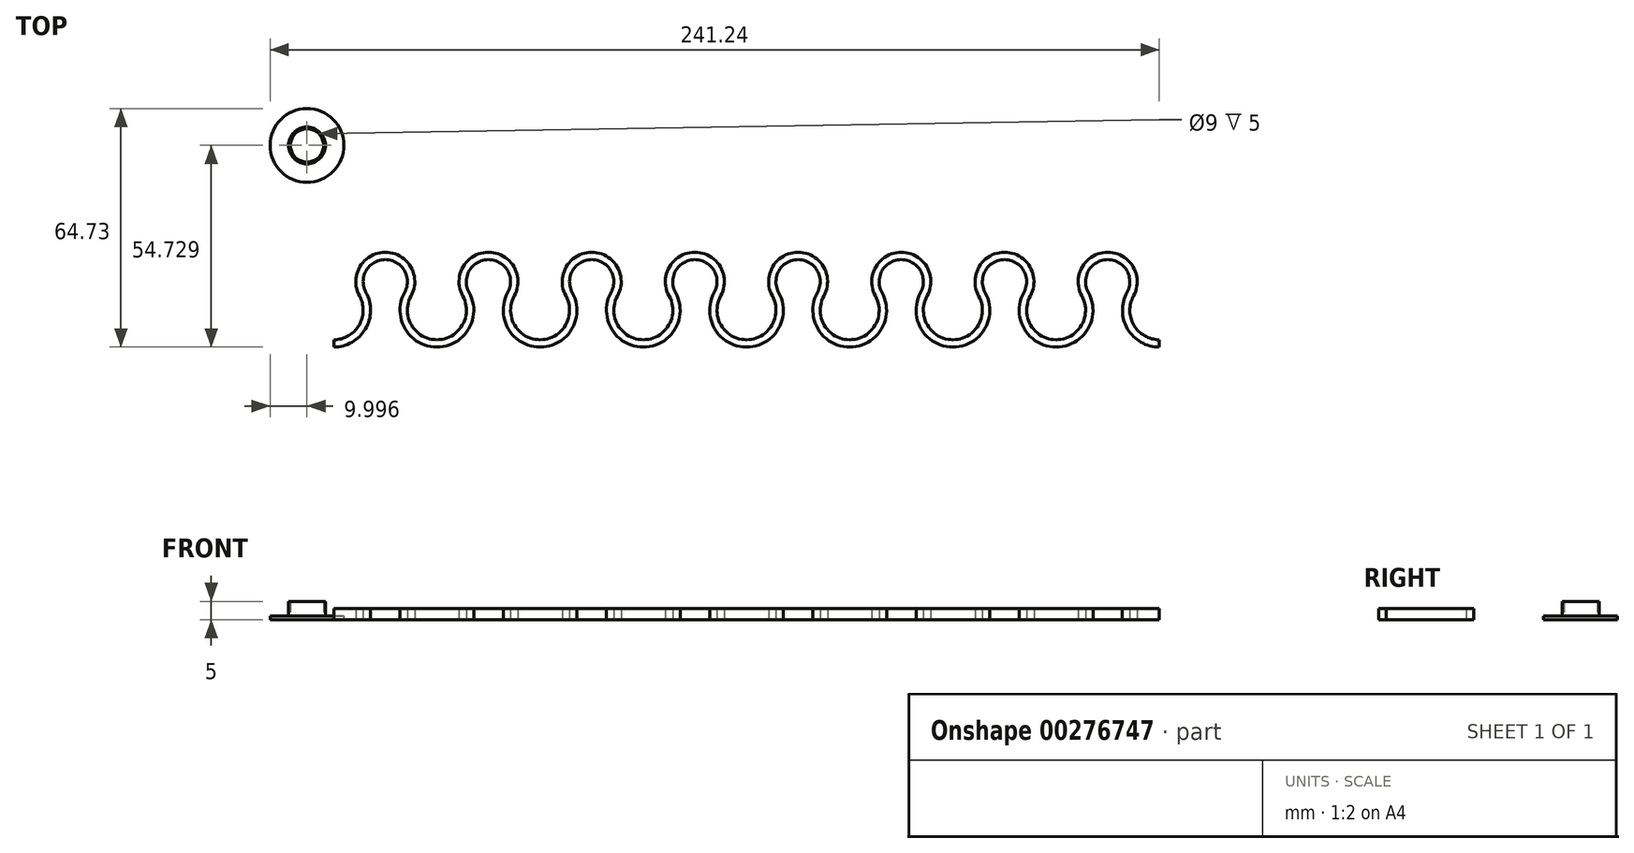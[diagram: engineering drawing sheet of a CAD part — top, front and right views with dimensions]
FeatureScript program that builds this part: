
annotation { "Feature Type Name" : "Feature", "Feature Type Description" : "" }
export const myFeature = defineFeature(function(context is Context, id is Id, definition is map)
    precondition{}
    {
        {
            var Q0;
            Q0=qCreatedBy(makeId("Top.planeOp"),FACE);
            var sketch = newSketch(context, id + "F0", { "sketchPlane" : qUnion([Q0])});
            skPoint(sketch, "E0", {"position": v(14, 0) * mm});
            skPoint(sketch, "E1", {"position": v(28, 0) * mm});
            skArc(sketch, "E2", {"start": v(0, 0) * mm, "mid": v(7, 11.87) * mm, "end": v(14, 0) * mm});
            skArc(sketch, "E3", {"start": v(14, 0) * mm, "mid": v(21, -11.87) * mm, "end": v(28, 0) * mm});
            skArc(sketch, "E4.1.0.0", {"start": v(28, 0) * mm, "mid": v(35, 11.87) * mm, "end": v(42, 0) * mm});
            skArc(sketch, "E4.1.0.1", {"start": v(42, 0) * mm, "mid": v(49, -11.87) * mm, "end": v(56, 0) * mm});
            skArc(sketch, "E4.2.0.0", {"start": v(56, 0) * mm, "mid": v(63, 11.87) * mm, "end": v(70, 0) * mm});
            skArc(sketch, "E4.2.0.1", {"start": v(70, 0) * mm, "mid": v(77, -11.87) * mm, "end": v(84, 0) * mm});
            skArc(sketch, "E4.3.0.0", {"start": v(84, 0) * mm, "mid": v(91, 11.87) * mm, "end": v(98, 0) * mm});
            skArc(sketch, "E4.3.0.1", {"start": v(98, 0) * mm, "mid": v(105, -11.87) * mm, "end": v(112, 0) * mm});
            skArc(sketch, "E4.4.0.0", {"start": v(112, 0) * mm, "mid": v(119, 11.87) * mm, "end": v(126, 0) * mm});
            skArc(sketch, "E4.4.0.1", {"start": v(126, 0) * mm, "mid": v(133, -11.87) * mm, "end": v(140, 0) * mm});
            skArc(sketch, "E4.5.0.0", {"start": v(140, 0) * mm, "mid": v(147, 11.87) * mm, "end": v(154, 0) * mm});
            skArc(sketch, "E4.5.0.1", {"start": v(154, 0) * mm, "mid": v(161, -11.87) * mm, "end": v(168, 0) * mm});
            skArc(sketch, "E4.6.0.0", {"start": v(168, 0) * mm, "mid": v(175, 11.87) * mm, "end": v(182, 0) * mm});
            skArc(sketch, "E4.6.0.1", {"start": v(182, 0) * mm, "mid": v(189, -11.87) * mm, "end": v(196, 0) * mm});
            skArc(sketch, "E4.7.0.0", {"start": v(196, 0) * mm, "mid": v(203, 11.87) * mm, "end": v(210, 0) * mm});
            skArc(sketch, "E4.7.0.1", {"start": v(210, 0) * mm, "mid": v(217, -11.87) * mm, "end": v(224, 0) * mm});
            skArc(sketch, "E4.8.0.0", {"start": v(224, 0) * mm, "mid": v(231, 11.87) * mm, "end": v(238, 0) * mm});
            skArc(sketch, "E4.8.0.1", {"start": v(238, 0) * mm, "mid": v(245, -11.87) * mm, "end": v(252, 0) * mm});
            skArc(sketch, "E4.9.0.0", {"start": v(252, 0) * mm, "mid": v(259, 11.87) * mm, "end": v(266, 0) * mm});
            skArc(sketch, "E4.9.0.1", {"start": v(266, 0) * mm, "mid": v(273, -11.87) * mm, "end": v(280, 0) * mm});
            skLineSegment(sketch, "E4.direction1", {"start": v(0, 0) * mm, "end": v(28, 0) * mm, "construction": true});
            skArc(sketch, "E5.0", {"start": v(264.25, 0.97) * mm, "mid": v(273, -13.87) * mm, "end": v(281.75, 0.97) * mm});
            skArc(sketch, "E5.1", {"start": v(253.75, 0.97) * mm, "mid": v(259, 9.87) * mm, "end": v(264.25, 0.97) * mm});
            skArc(sketch, "E5.2", {"start": v(236.25, 0.97) * mm, "mid": v(245, -13.87) * mm, "end": v(253.75, 0.97) * mm});
            skArc(sketch, "E5.3", {"start": v(225.75, 0.97) * mm, "mid": v(231, 9.87) * mm, "end": v(236.25, 0.97) * mm});
            skArc(sketch, "E5.4", {"start": v(208.25, 0.97) * mm, "mid": v(217, -13.87) * mm, "end": v(225.75, 0.97) * mm});
            skArc(sketch, "E5.5", {"start": v(197.75, 0.97) * mm, "mid": v(203, 9.87) * mm, "end": v(208.25, 0.97) * mm});
            skArc(sketch, "E5.6", {"start": v(180.25, 0.97) * mm, "mid": v(189, -13.87) * mm, "end": v(197.75, 0.97) * mm});
            skArc(sketch, "E5.7", {"start": v(169.75, 0.97) * mm, "mid": v(175, 9.87) * mm, "end": v(180.25, 0.97) * mm});
            skArc(sketch, "E5.8", {"start": v(152.25, 0.97) * mm, "mid": v(161, -13.87) * mm, "end": v(169.75, 0.97) * mm});
            skArc(sketch, "E5.9", {"start": v(57.75, 0.97) * mm, "mid": v(63, 9.87) * mm, "end": v(68.25, 0.97) * mm});
            skArc(sketch, "E5.10", {"start": v(40.25, 0.97) * mm, "mid": v(49, -13.87) * mm, "end": v(57.75, 0.97) * mm});
            skArc(sketch, "E5.11", {"start": v(29.75, 0.97) * mm, "mid": v(35, 9.87) * mm, "end": v(40.25, 0.97) * mm});
            skArc(sketch, "E5.12", {"start": v(12.25, 0.97) * mm, "mid": v(21, -13.87) * mm, "end": v(29.75, 0.97) * mm});
            skArc(sketch, "E5.13", {"start": v(68.25, 0.97) * mm, "mid": v(77, -13.87) * mm, "end": v(85.75, 0.97) * mm});
            skArc(sketch, "E5.14", {"start": v(85.75, 0.97) * mm, "mid": v(91, 9.87) * mm, "end": v(96.25, 0.97) * mm});
            skArc(sketch, "E5.15", {"start": v(96.25, 0.97) * mm, "mid": v(105, -13.87) * mm, "end": v(113.75, 0.97) * mm});
            skArc(sketch, "E5.16", {"start": v(113.75, 0.97) * mm, "mid": v(119, 9.87) * mm, "end": v(124.25, 0.97) * mm});
            skArc(sketch, "E5.17", {"start": v(124.25, 0.97) * mm, "mid": v(133, -13.87) * mm, "end": v(141.75, 0.97) * mm});
            skArc(sketch, "E5.18", {"start": v(141.75, 0.97) * mm, "mid": v(147, 9.87) * mm, "end": v(152.25, 0.97) * mm});
            skLineSegment(sketch, "E6", {"start": v(21, -3.87) * mm, "end": v(21, -64.76) * mm});
            skPoint(sketch, "E6.endSnap0", {"position": v(21, -11.87) * mm});
            skLineSegment(sketch, "E7", {"start": v(21, -64.76) * mm, "end": v(273, -64.76) * mm});
            skLineSegment(sketch, "E8", {"start": v(273, -3.87) * mm, "end": v(273, -64.76) * mm});
            skLineSegment(sketch, "E9", {"start": v(245, -3.87) * mm, "end": v(245, -64.76) * mm});
            skPoint(sketch, "E9.endSnap0", {"position": v(245, -11.87) * mm});
            skLineSegment(sketch, "E10", {"start": v(245, -64.76) * mm, "end": v(246.72, -66.87) * mm});
            skSolve(sketch);
        }
        {
            var Q0;
            {var subQ1=sQuery(id+"F0.wireOp",EDGE,"E5.3");Q0=makeQuery(id+"F0.imprint","IMPRINT",FACE,{"disambiguationData":[TD([[makeQuery(id+"F0.imprint","IMPRINT",EDGE,{"derivedFrom":subQ1}),-1.0]])]});}
            extrude(context, id + "F1", {"entities" : qUnion([Q0]), "depth" : 3 * mm});
        }
        {
            var Q0;
            Q0=qCreatedBy(makeId("Top.planeOp"),FACE);
            var sketch = newSketch(context, id + "F2", { "sketchPlane" : qUnion([Q0])});
            skCircle(sketch, "E11", {"center": v(13.76, 40.86) * mm, "radius": 10 * mm});
            skCircle(sketch, "E12", {"center": v(13.76, 40.86) * mm, "radius": 5 * mm});
            skCircle(sketch, "E13", {"center": v(13.76, 40.86) * mm, "radius": 4.5 * mm});
            skSolve(sketch);
        }
        {
            var Q0;
            Q0=makeQuery(id+"F2.imprint","IMPRINT",FACE,{"disambiguationData":[TD([[makeQuery(id+"F2.imprint","IMPRINT",EDGE,{"derivedFrom":sQuery(id+"F2.wireOp",EDGE,"E11")}),1.0]])]});
            extrude(context, id + "F3", {"entities" : qUnion([Q0]), "depth" : 1 * mm});
        }
        {
            var Q0;
            Q0=makeQuery(id+"F2.imprint","IMPRINT",FACE,{"disambiguationData":[TD([[makeQuery(id+"F2.imprint","IMPRINT",EDGE,{"derivedFrom":sQuery(id+"F2.wireOp",EDGE,"E12")}),1.0]])]});
            extrude(context, id + "F4", {"entities" : qUnion([Q0]), "operationType" : NewBodyOperationType.ADD, "depth" : 5 * mm});
        }
    });
